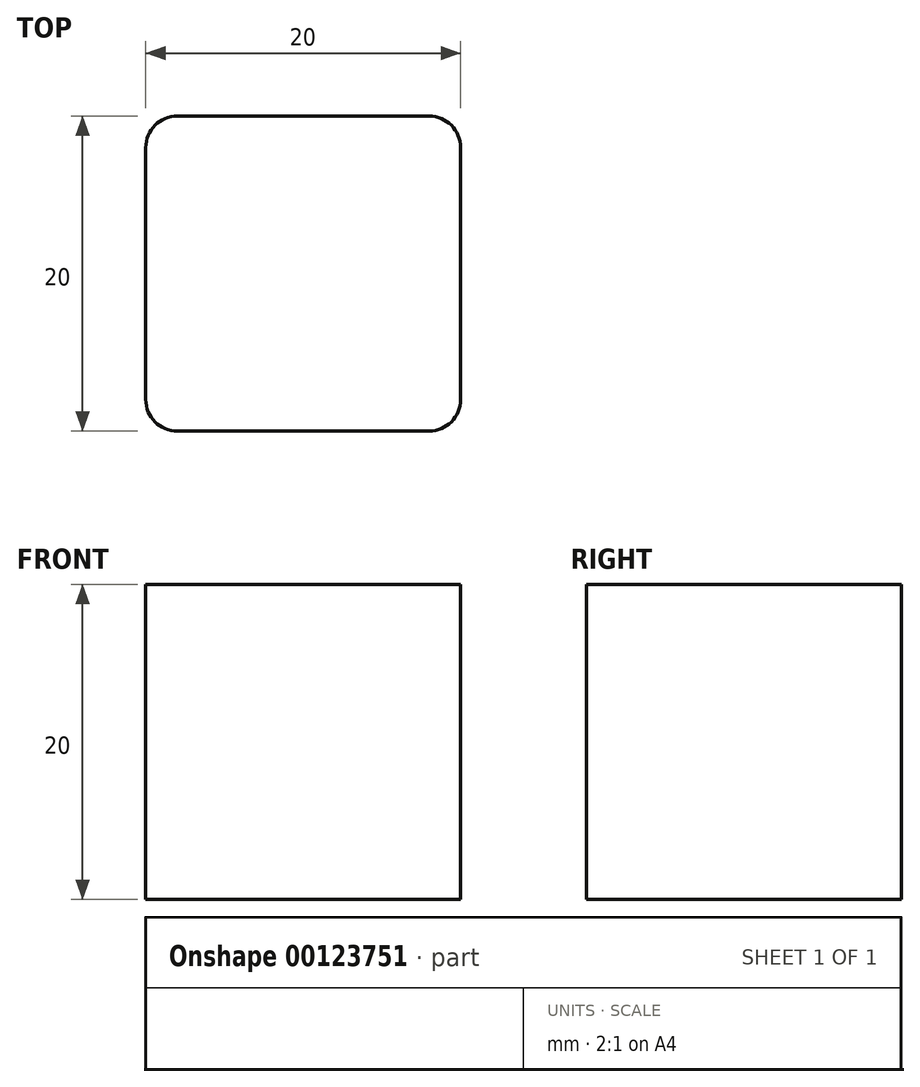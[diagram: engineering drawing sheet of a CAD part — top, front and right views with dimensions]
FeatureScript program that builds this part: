
annotation { "Feature Type Name" : "Feature", "Feature Type Description" : "" }
export const myFeature = defineFeature(function(context is Context, id is Id, definition is map)
    precondition{}
    {
        {
            var Q0;
            Q0=qCreatedBy(makeId("Top.planeOp"),FACE);
            var sketch = newSketch(context, id + "F0", { "sketchPlane" : qUnion([Q0])});
            skLineSegment(sketch, "E0.bottom", {"start": v(0, 0) * mm, "end": v(20, 0) * mm});
            skLineSegment(sketch, "E0.top", {"start": v(0, 20) * mm, "end": v(20, 20) * mm});
            skLineSegment(sketch, "E0.left", {"start": v(0, 0) * mm, "end": v(0, 20) * mm});
            skLineSegment(sketch, "E0.right", {"start": v(20, 0) * mm, "end": v(20, 20) * mm});
            skSolve(sketch);
        }
        {
            var Q0;
            Q0=makeQuery(id+"F0.imprint","IMPRINT",FACE,{"disambiguationData":[TD([[makeQuery(id+"F0.imprint","IMPRINT",EDGE,{"derivedFrom":sQuery(id+"F0.wireOp",EDGE,"E0.bottom")}),1.0]])]});
            extrude(context, id + "F1", {"entities" : qUnion([Q0]), "depth" : 20 * mm});
        }
        {
            var Q0;
            Q0=makeQuery(id+"F1.opExtrude","SWEPT_EDGE",EDGE,{"disambiguationData":[OSD([sQuery(id+"F0.wireOp",EDGE,"E0.top"),sQuery(id+"F0.wireOp",EDGE,"E0.right")])]});
            var Q1;
            Q1=makeQuery(id+"F1.opExtrude","SWEPT_EDGE",EDGE,{"disambiguationData":[OSD([sQuery(id+"F0.wireOp",EDGE,"E0.top"),sQuery(id+"F0.wireOp",EDGE,"E0.left")])]});
            var Q2;
            Q2=makeQuery(id+"F1.opExtrude","SWEPT_EDGE",EDGE,{"disambiguationData":[OSD([sQuery(id+"F0.wireOp",EDGE,"E0.bottom"),sQuery(id+"F0.wireOp",EDGE,"E0.right")])]});
            var Q3;
            Q3=makeQuery(id+"F1.opExtrude","SWEPT_EDGE",EDGE,{"disambiguationData":[OSD([sQuery(id+"F0.wireOp",EDGE,"E0.bottom"),sQuery(id+"F0.wireOp",EDGE,"E0.left")])]});
            fillet(context, id + "F2", {"entities" : qUnion([Q0, Q1, Q2, Q3]), "radius" : 2 * mm, "tangentPropagation" : true, "allowEdgeOverflow" : false});
        }
    });
